# Revit family: Towel_Bar-American_Standard-Contemporary_CS_Series-8335.024_Series
name_source: partatom
category: Specialty Equipment
revit_build: Autodesk Revit 2018 (Build: 20170223_1515(x64)
units: mm (PartAtom-declared; Revit-internal decimal feet)

## family parameters
Cut with Voids When Loaded = No
Host = Face
OmniClass Number = 23.40.20.21.27
OmniClass Title = Towel Bars
Part Type = Normal
Room Calculation Point = No
Round Connector Dimension = Use Diameter
Shared = Yes

## types (2) — shared parameters
Assembly Code = C1030200
Default Elevation = 40"
Height = 2"
Installation Type = Wall Mounted
Length = 4 1/2"
Manufacturer = American Standard
Price = Prices may vary. Please consult Manufacturer Representative for most up-to-date price list.
Product Documentation Link = https://americanstandard.box.com
Product Page URL = https://www.americanstandard-us.com
Revised Date = 03/22/2022
URL = http://www.americanstandard-us.com
Width = 24"

## per-type parameters (varying)
| type | Description | Finish | Material |
| 8335024.002 | CS Series 24" Towel Bar Polished Chrome | Brass-American Standard-002-Polished Chrome | Brass-American Standard-002-Polished Chrome |
| 8335024.295 | CS Series 24" Towel Bar | Brass-American Standard-295-Satin Nickel | Brass-American Standard-295-Satin Nickel |

note: column(s) folded — value = type name in every type: Model

## geometry (parser evidence)
native form markers: Sweep x3
no freeform markers — native parametric forms only
